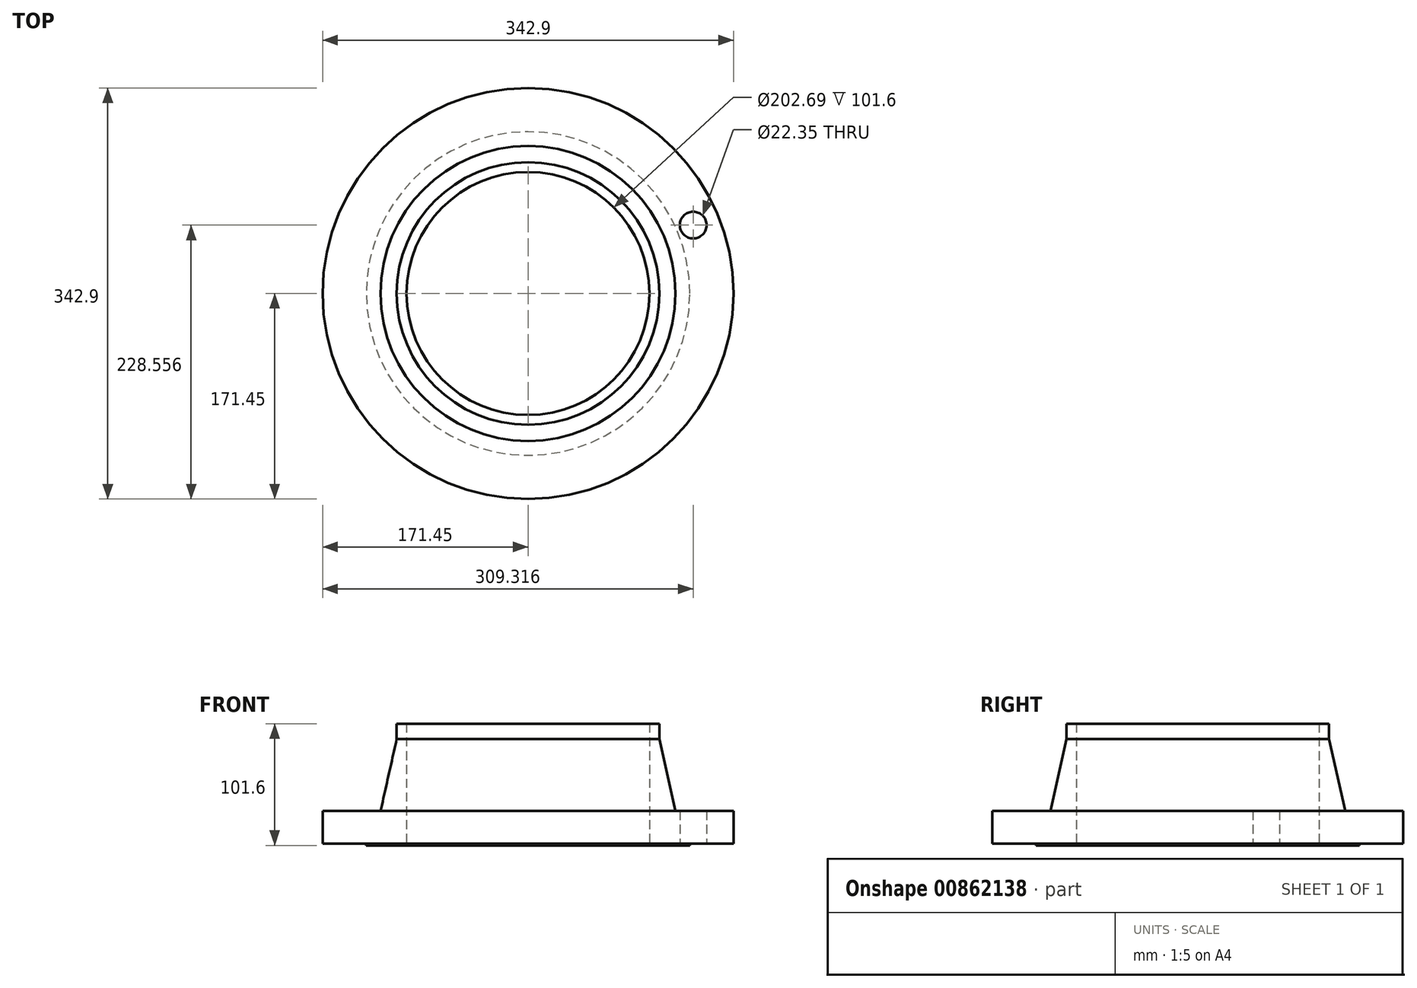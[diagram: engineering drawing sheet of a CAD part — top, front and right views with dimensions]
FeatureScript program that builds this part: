
annotation { "Feature Type Name" : "Feature", "Feature Type Description" : "" }
export const myFeature = defineFeature(function(context is Context, id is Id, definition is map)
    precondition{}
    {
        {
            var Q0;
            Q0=qCreatedBy(makeId("Front.planeOp"),FACE);
            var sketch = newSketch(context, id + "F0", { "sketchPlane" : qUnion([Q0])});
            skLineSegment(sketch, "E0", {"start": v(101.35, 0) * mm, "end": v(135, 0) * mm});
            skLineSegment(sketch, "E1", {"start": v(135, 0) * mm, "end": v(135, 1.59) * mm});
            skLineSegment(sketch, "E2", {"start": v(135, 1.59) * mm, "end": v(171.45, 1.59) * mm});
            skLineSegment(sketch, "E3", {"start": v(171.45, 1.59) * mm, "end": v(171.45, 28.7) * mm});
            skLineSegment(sketch, "E4", {"start": v(171.45, 28.7) * mm, "end": v(123.06, 28.7) * mm});
            skLineSegment(sketch, "E5", {"start": v(123.06, 28.7) * mm, "end": v(109.6, 88.9) * mm});
            skLineSegment(sketch, "E6", {"start": v(109.6, 88.9) * mm, "end": v(109.6, 101.6) * mm});
            skLineSegment(sketch, "E7", {"start": v(109.6, 101.6) * mm, "end": v(101.35, 101.6) * mm});
            skLineSegment(sketch, "E8", {"start": v(101.35, 101.6) * mm, "end": v(101.35, 0) * mm});
            skLineSegment(sketch, "E9", {"start": v(0, 0) * mm, "end": v(0, 101.6) * mm, "construction": true});
            skSolve(sketch);
        }
        {
            var Q0;
            Q0=qCreatedBy(makeId("Top.planeOp"),FACE);
            var sketch = newSketch(context, id + "F1", { "sketchPlane" : qUnion([Q0])});
            skLineSegment(sketch, "E10", {"start": v(0, 0) * mm, "end": v(137.87, 57.1) * mm, "construction": true});
            skLineSegment(sketch, "E11", {"start": v(149.23, 0) * mm, "end": v(0, 0) * mm, "construction": true});
            skCircle(sketch, "E12", {"center": v(0, 0) * mm, "radius": 149.23 * mm, "construction": true});
            skCircle(sketch, "E13", {"center": v(137.87, 57.1) * mm, "radius": 11.18 * mm});
            skSolve(sketch);
        }
        {
            var Q0;
            Q0=makeQuery(id+"F0.imprint","IMPRINT",FACE,{"disambiguationData":[TD([[makeQuery(id+"F0.imprint","IMPRINT",EDGE,{"derivedFrom":sQuery(id+"F0.wireOp",EDGE,"E0")}),1.0]])]});
            var Q1;
            Q1=sQuery(id+"F0.wireOp",EDGE,"E8");
            var Q2;
            Q2=sQuery(id+"F0.wireOp",EDGE,"E7");
            var Q3;
            Q3=sQuery(id+"F0.wireOp",EDGE,"E6");
            var Q4;
            Q4=sQuery(id+"F0.wireOp",EDGE,"E5");
            var Q5;
            Q5=sQuery(id+"F0.wireOp",EDGE,"E9");
            revolve(context, id + "F2", {"surfaceOperationType" : NewSurfaceOperationType.NEW, "entities" : qUnion([Q0]), "surfaceEntities" : qUnion([Q1, Q2, Q3, Q4]), "axis" : qUnion([Q5]), "revolveType" : RevolveType.FULL});
        }
        {
            var Q0;
            Q0 = qSketchRegion(id + "F1", true);
            extrude(context, id + "F3", {"entities" : qUnion([Q0]), "operationType" : NewBodyOperationType.REMOVE, "endBound" : BoundingType.THROUGH_ALL, "depth" : 25.4 * mm, "offsetDistance" : 25.4 * mm});
        }
    });
